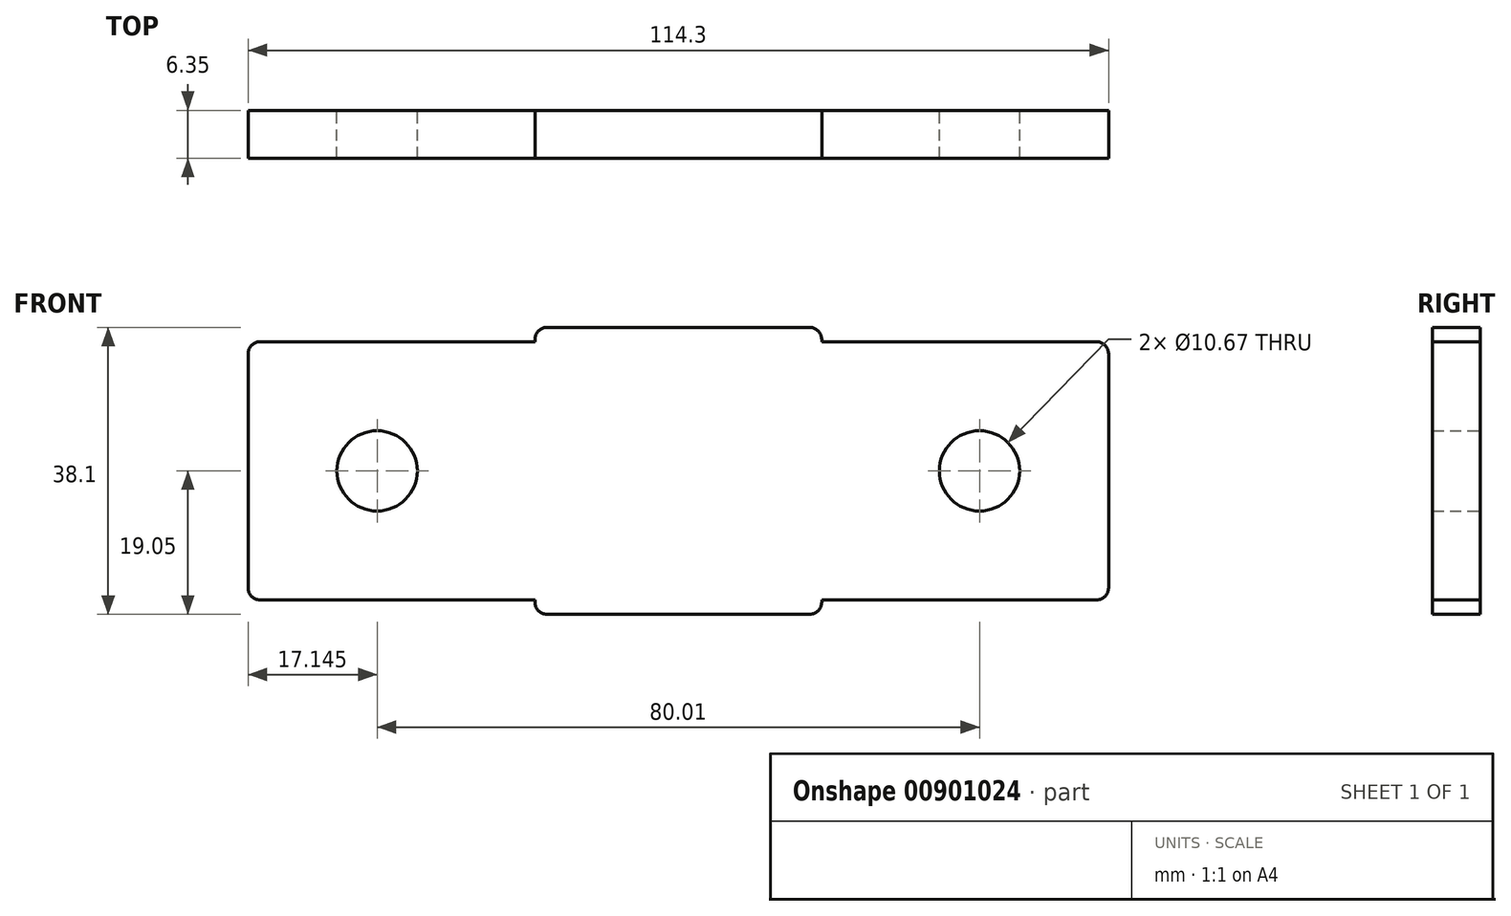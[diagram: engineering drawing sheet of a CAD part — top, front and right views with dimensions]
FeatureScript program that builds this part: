
annotation { "Feature Type Name" : "Feature", "Feature Type Description" : "" }
export const myFeature = defineFeature(function(context is Context, id is Id, definition is map)
    precondition{}
    {
        {
            var Q0;
            Q0=qCreatedBy(makeId("Front.planeOp"),FACE);
            var sketch = newSketch(context, id + "F0", { "sketchPlane" : qUnion([Q0])});
            skLineSegment(sketch, "E0.bottom", {"start": v(1.59, 0) * mm, "end": v(36.51, 0) * mm});
            skLineSegment(sketch, "E0.top", {"start": v(1.59, -38.1) * mm, "end": v(36.51, -38.1) * mm});
            skLineSegment(sketch, "E0.left", {"start": v(0, -1.59) * mm, "end": v(0, -1.9) * mm});
            skLineSegment(sketch, "E0.right", {"start": v(38.1, -1.59) * mm, "end": v(38.1, -1.9) * mm});
            skLineSegment(sketch, "E1", {"start": v(0, -1.9) * mm, "end": v(-36.51, -1.9) * mm});
            skLineSegment(sketch, "E2", {"start": v(-38.1, -3.5) * mm, "end": v(-38.1, -34.6) * mm});
            skLineSegment(sketch, "E3", {"start": v(-36.51, -36.2) * mm, "end": v(0, -36.2) * mm});
            skLineSegment(sketch, "E4", {"start": v(38.1, -1.9) * mm, "end": v(74.61, -1.9) * mm});
            skLineSegment(sketch, "E5", {"start": v(76.2, -3.5) * mm, "end": v(76.2, -34.6) * mm});
            skLineSegment(sketch, "E6", {"start": v(74.61, -36.2) * mm, "end": v(38.1, -36.2) * mm});
            skPoint(sketch, "E7.visualSharp", {"position": v(76.2, -1.9) * mm});
            skArc(sketch, "E7.filletArc", {"start": v(76.2, -3.5) * mm, "mid": v(75.74, -2.37) * mm, "end": v(74.61, -1.9) * mm});
            skPoint(sketch, "E8.visualSharp", {"position": v(76.2, -36.2) * mm});
            skArc(sketch, "E8.filletArc", {"start": v(74.61, -36.2) * mm, "mid": v(75.74, -35.73) * mm, "end": v(76.2, -34.6) * mm});
            skLineSegment(sketch, "E9.trimOffspring", {"start": v(38.1, -36.2) * mm, "end": v(38.1, -36.51) * mm});
            skLineSegment(sketch, "E10.trimOffspring", {"start": v(0, -36.2) * mm, "end": v(0, -36.51) * mm});
            skPoint(sketch, "E11.visualSharp", {"position": v(38.1, 0) * mm});
            skArc(sketch, "E11.filletArc", {"start": v(38.1, -1.59) * mm, "mid": v(37.64, -0.46) * mm, "end": v(36.51, 0) * mm});
            skPoint(sketch, "E12.visualSharp", {"position": v(38.1, -38.1) * mm});
            skArc(sketch, "E12.filletArc", {"start": v(36.51, -38.1) * mm, "mid": v(37.64, -37.64) * mm, "end": v(38.1, -36.51) * mm});
            skPoint(sketch, "E13.visualSharp", {"position": v(0, -38.1) * mm});
            skArc(sketch, "E13.filletArc", {"start": v(0, -36.51) * mm, "mid": v(0.46, -37.64) * mm, "end": v(1.59, -38.1) * mm});
            skPoint(sketch, "E14.visualSharp", {"position": v(0, 0) * mm});
            skArc(sketch, "E14.filletArc", {"start": v(1.59, 0) * mm, "mid": v(0.46, -0.46) * mm, "end": v(0, -1.59) * mm});
            skPoint(sketch, "E15.visualSharp", {"position": v(-38.1, -1.9) * mm});
            skArc(sketch, "E15.filletArc", {"start": v(-36.51, -1.9) * mm, "mid": v(-37.64, -2.37) * mm, "end": v(-38.1, -3.5) * mm});
            skPoint(sketch, "E16.visualSharp", {"position": v(-38.1, -36.2) * mm});
            skArc(sketch, "E16.filletArc", {"start": v(-38.1, -34.6) * mm, "mid": v(-37.64, -35.73) * mm, "end": v(-36.51, -36.2) * mm});
            skCircle(sketch, "E17", {"center": v(59.05, -19.05) * mm, "radius": 5.33 * mm});
            skCircle(sketch, "E18", {"center": v(-20.95, -19.05) * mm, "radius": 5.33 * mm});
            skSolve(sketch);
        }
        {
            var Q0;
            Q0 = qSketchRegion(id + "F0", true);
            extrude(context, id + "F1", {"entities" : qUnion([Q0]), "flatOperationType" : FlatOperationType.REMOVE, "depth" : 6.35 * mm, "offsetDistance" : 25.4 * mm, "domain" : OperationDomain.MODEL});
        }
    });
